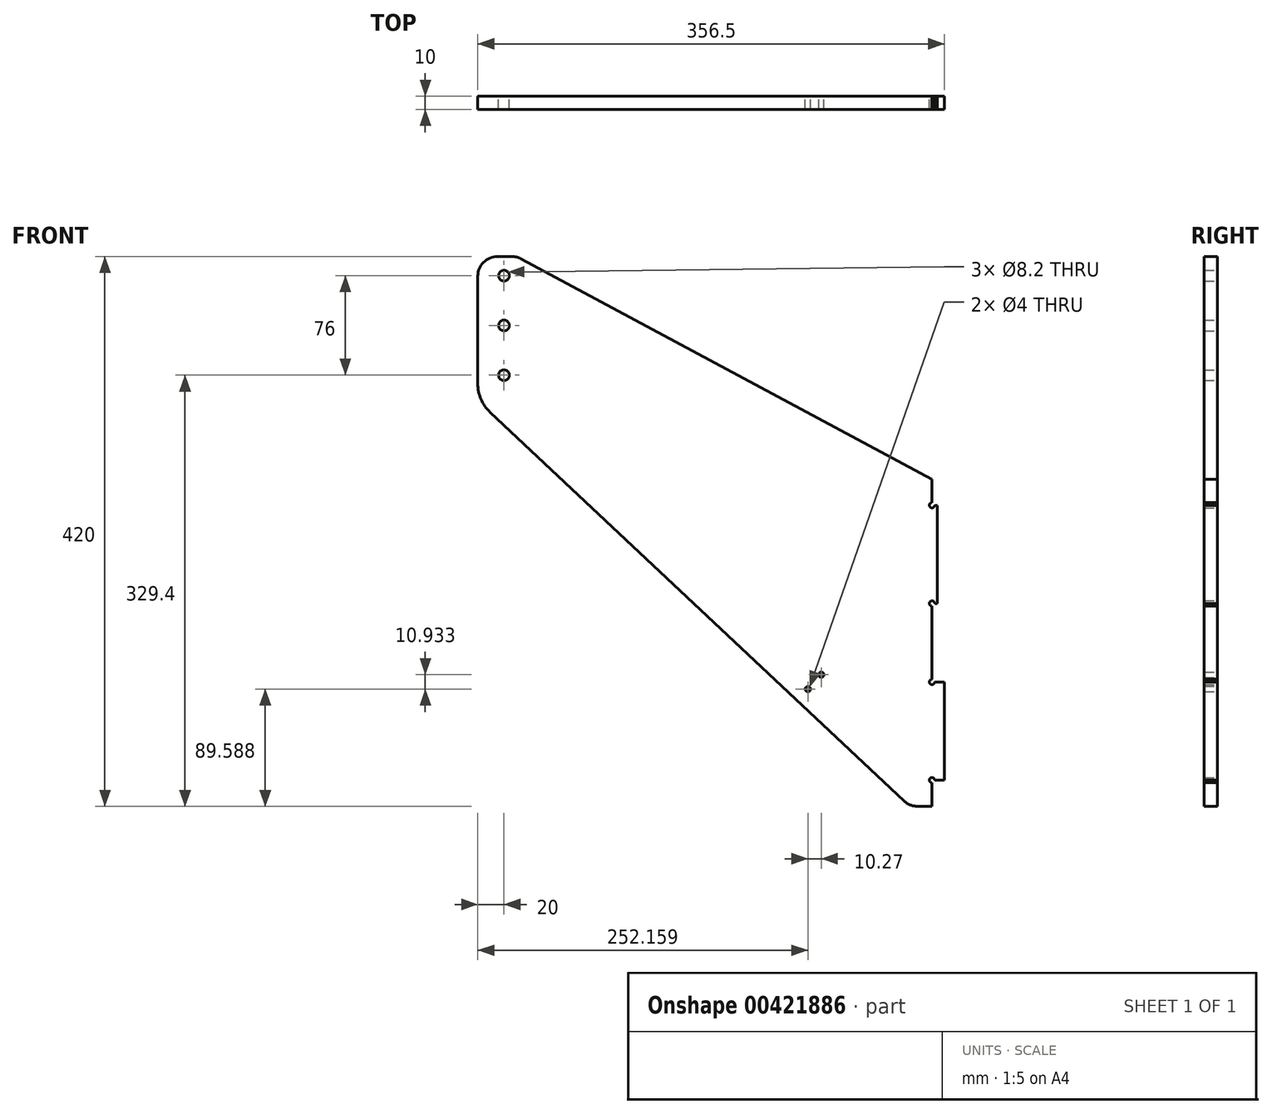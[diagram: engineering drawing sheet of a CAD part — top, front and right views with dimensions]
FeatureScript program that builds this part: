
annotation { "Feature Type Name" : "Feature", "Feature Type Description" : "" }
export const myFeature = defineFeature(function(context is Context, id is Id, definition is map)
    precondition{}
    {
        {
            var Q0;
            Q0=qCreatedBy(makeId("Front.planeOp"),FACE);
            var sketch = newSketch(context, id + "F0", { "sketchPlane" : qUnion([Q0])});
            skLineSegment(sketch, "E0", {"start": v(0, 0) * mm, "end": v(0, 519.12) * mm, "construction": true});
            skLineSegment(sketch, "E1", {"start": v(0, 0) * mm, "end": v(526.4, 0) * mm, "construction": true});
            skLineSegment(sketch, "E2", {"start": v(330, 0) * mm, "end": v(347, 0) * mm});
            skLineSegment(sketch, "E3", {"start": v(347, 0) * mm, "end": v(347, 18) * mm});
            skLineSegment(sketch, "E4", {"start": v(349, 20) * mm, "end": v(356.5, 20) * mm});
            skCircle(sketch, "E5", {"center": v(20, 329.4) * mm, "radius": 4.1 * mm});
            skCircle(sketch, "E6", {"center": v(20, 367.4) * mm, "radius": 4.1 * mm});
            skCircle(sketch, "E7", {"center": v(20, 405.4) * mm, "radius": 4.1 * mm});
            skLineSegment(sketch, "E8", {"start": v(347, 97) * mm, "end": v(347, 153) * mm});
            skLineSegment(sketch, "E9", {"start": v(349, 230) * mm, "end": v(351, 230) * mm});
            skLineSegment(sketch, "E10", {"start": v(351, 230) * mm, "end": v(351, 155) * mm});
            skLineSegment(sketch, "E11", {"start": v(356.5, 20) * mm, "end": v(356.5, 95) * mm});
            skLineSegment(sketch, "E12", {"start": v(351, 155) * mm, "end": v(349, 155) * mm});
            skLineSegment(sketch, "E13", {"start": v(356.5, 95) * mm, "end": v(349, 95) * mm});
            skLineSegment(sketch, "E14.trimOffspring", {"start": v(347, 232) * mm, "end": v(347, 250) * mm});
            skLineSegment(sketch, "E15", {"start": v(0, 420) * mm, "end": v(0, 310) * mm});
            skLineSegment(sketch, "E16", {"start": v(330, 0) * mm, "end": v(0, 310) * mm});
            skLineSegment(sketch, "E17", {"start": v(243.94, 80.84) * mm, "end": v(267.17, 105.57) * mm, "construction": true});
            skCircle(sketch, "E18", {"center": v(252.16, 89.59) * mm, "radius": 2 * mm});
            skCircle(sketch, "E19", {"center": v(262.43, 100.52) * mm, "radius": 2 * mm});
            skLineSegment(sketch, "E20", {"start": v(0, 420) * mm, "end": v(30, 420) * mm});
            skLineSegment(sketch, "E21", {"start": v(30, 420) * mm, "end": v(347, 250) * mm});
            skArc(sketch, "E22", {"start": v(347, 232) * mm, "mid": v(345.59, 228.59) * mm, "end": v(349, 230) * mm});
            skArc(sketch, "E23", {"start": v(347, 97) * mm, "mid": v(345.59, 93.59) * mm, "end": v(349, 95) * mm});
            skArc(sketch, "E24", {"start": v(349, 20) * mm, "mid": v(345.59, 21.41) * mm, "end": v(347, 18) * mm});
            skArc(sketch, "E25", {"start": v(349, 155) * mm, "mid": v(345.59, 156.41) * mm, "end": v(347, 153) * mm});
            skSolve(sketch);
        }
        {
            var Q0;
            Q0=makeQuery(id+"F0.imprint","IMPRINT",FACE,{"disambiguationData":[TD([[makeQuery(id+"F0.imprint","IMPRINT",EDGE,{"derivedFrom":sQuery(id+"F0.wireOp",EDGE,"E2")}),1.0]])]});
            extrude(context, id + "F1", {"entities" : qUnion([Q0]), "depth" : 10 * mm});
        }
        {
            var Q0;
            Q0=makeQuery(id+"F1.opExtrude","SWEPT_EDGE",EDGE,{"disambiguationData":[OSD([sQuery(id+"F0.wireOp",EDGE,"E15"),sQuery(id+"F0.wireOp",EDGE,"E16")])]});
            fillet(context, id + "F2", {"entities" : qUnion([Q0]), "radius" : 30 * mm, "tangentPropagation" : true, "allowEdgeOverflow" : false});
        }
        {
            var Q0;
            Q0=makeQuery(id+"F1.opExtrude","SWEPT_EDGE",EDGE,{"disambiguationData":[OSD([sQuery(id+"F0.wireOp",EDGE,"E15"),sQuery(id+"F0.wireOp",EDGE,"E20")])]});
            var Q1;
            Q1=makeQuery(id+"F1.opExtrude","SWEPT_EDGE",EDGE,{"disambiguationData":[OSD([sQuery(id+"F0.wireOp",EDGE,"E20"),sQuery(id+"F0.wireOp",EDGE,"E21")])]});
            var Q2;
            Q2=makeQuery(id+"F1.opExtrude","SWEPT_EDGE",EDGE,{"disambiguationData":[OSD([sQuery(id+"F0.wireOp",EDGE,"E2"),sQuery(id+"F0.wireOp",EDGE,"E16")])]});
            fillet(context, id + "F3", {"entities" : qUnion([Q0, Q1, Q2]), "radius" : 15 * mm, "tangentPropagation" : true, "allowEdgeOverflow" : false});
        }
    });
